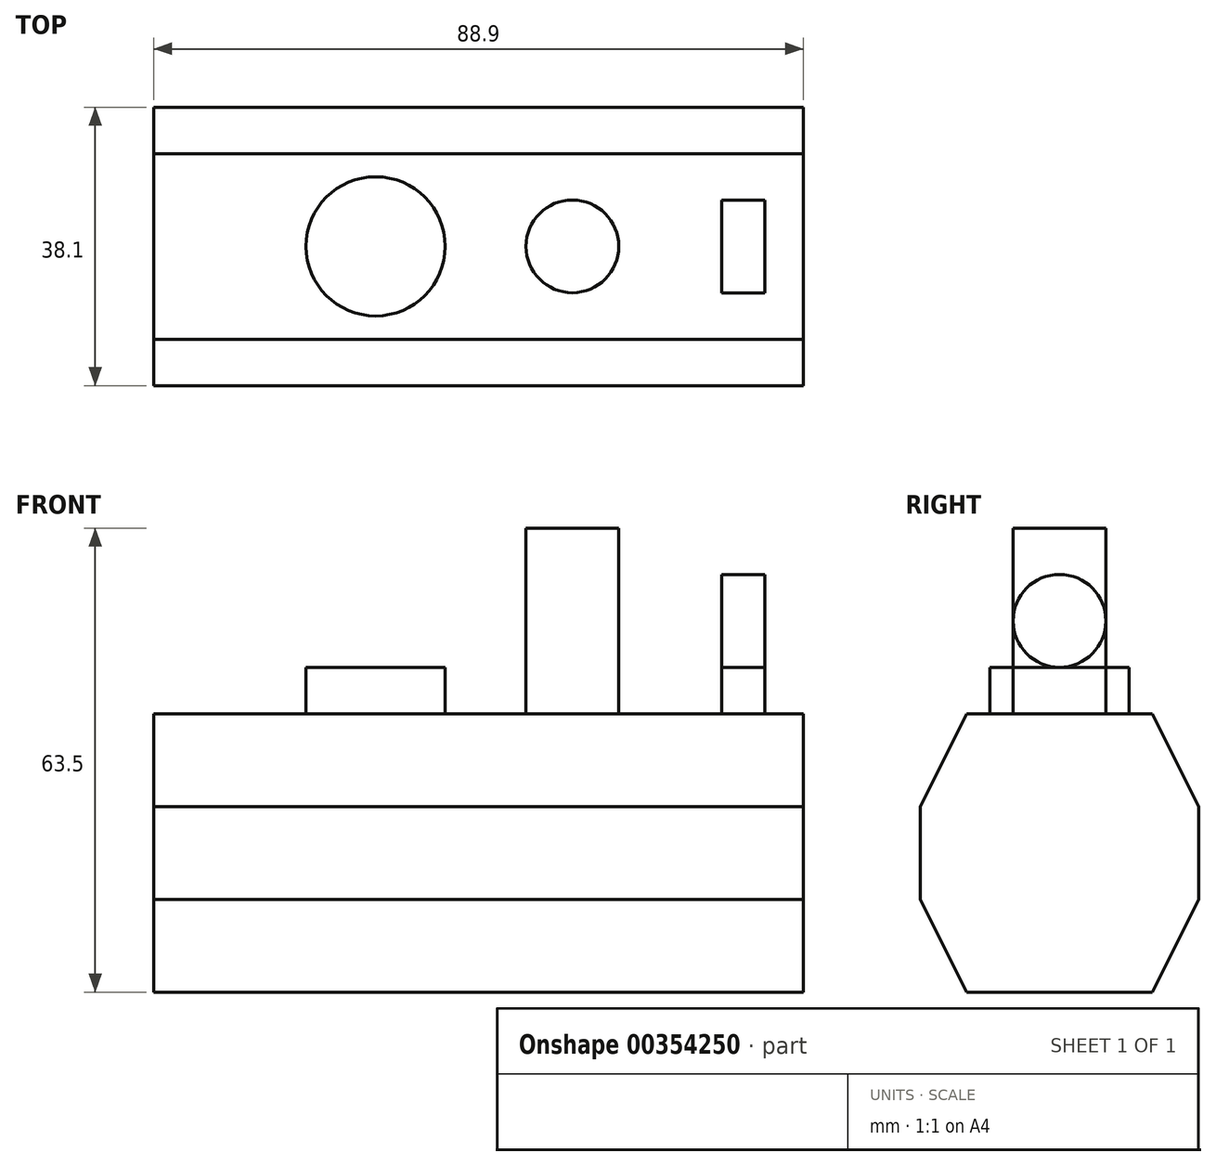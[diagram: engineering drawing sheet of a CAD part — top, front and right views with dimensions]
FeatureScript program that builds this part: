
annotation { "Feature Type Name" : "Feature", "Feature Type Description" : "" }
export const myFeature = defineFeature(function(context is Context, id is Id, definition is map)
    precondition{}
    {
        {
            var Q0;
            Q0=qCreatedBy(makeId("Front.planeOp"),FACE);
            var sketch = newSketch(context, id + "F0", { "sketchPlane" : qUnion([Q0])});
            skLineSegment(sketch, "E0.bottom", {"start": v(-41.2, 31.8) * mm, "end": v(47.7, 31.8) * mm});
            skLineSegment(sketch, "E0.top", {"start": v(-41.2, -6.3) * mm, "end": v(47.7, -6.3) * mm});
            skLineSegment(sketch, "E0.left", {"start": v(-41.2, 31.8) * mm, "end": v(-41.2, -6.3) * mm});
            skLineSegment(sketch, "E0.right", {"start": v(47.7, 31.8) * mm, "end": v(47.7, -6.3) * mm});
            skSolve(sketch);
        }
        {
            var Q0;
            Q0 = qSketchRegion(id + "F0", true);
            extrude(context, id + "F1", {"entities" : qUnion([Q0]), "depth" : 38.1 * mm});
        }
        {
            var Q0;
            Q0=makeQuery(id+"F1.opExtrude","SWEPT_FACE",FACE,{"disambiguationData":[OSD([sQuery(id+"F0.wireOp",EDGE,"E0.left")])]});
            var sketch = newSketch(context, id + "F2", { "sketchPlane" : qUnion([Q0])});
            skLineSegment(sketch, "E1", {"start": v(0, 19.1) * mm, "end": v(6.35, 31.8) * mm});
            skLineSegment(sketch, "E2", {"start": v(31.75, 31.8) * mm, "end": v(38.1, 19.1) * mm});
            skLineSegment(sketch, "E3", {"start": v(0, 6.4) * mm, "end": v(6.35, -6.3) * mm});
            skLineSegment(sketch, "E4", {"start": v(38.1, 6.4) * mm, "end": v(31.75, -6.3) * mm});
            skSolve(sketch);
        }
        {
            var Q0;
            {var subQ0=sQuery(id+"F2.wireOp",EDGE,"E1");Q0=makeQuery(id+"F2.imprint","IMPRINT",FACE,{"disambiguationData":[TD([[makeQuery(id+"F2.imprint","IMPRINT",EDGE,{"derivedFrom":subQ0}),1.0]])]});}
            var Q1;
            {var subQ0=sQuery(id+"F2.wireOp",EDGE,"E3");Q1=makeQuery(id+"F2.imprint","IMPRINT",FACE,{"disambiguationData":[TD([[makeQuery(id+"F2.imprint","IMPRINT",EDGE,{"derivedFrom":subQ0}),-1.0]])]});}
            var Q2;
            {var subQ0=sQuery(id+"F2.wireOp",EDGE,"E4");Q2=makeQuery(id+"F2.imprint","IMPRINT",FACE,{"disambiguationData":[TD([[makeQuery(id+"F2.imprint","IMPRINT",EDGE,{"derivedFrom":subQ0}),1.0]])]});}
            var Q3;
            {var subQ0=sQuery(id+"F2.wireOp",EDGE,"E2");Q3=makeQuery(id+"F2.imprint","IMPRINT",FACE,{"disambiguationData":[TD([[makeQuery(id+"F2.imprint","IMPRINT",EDGE,{"derivedFrom":subQ0}),1.0]])]});}
            extrude(context, id + "F3", {"entities" : qUnion([Q0, Q1, Q2, Q3]), "operationType" : NewBodyOperationType.REMOVE, "endBound" : BoundingType.THROUGH_ALL, "oppositeDirection" : true, "depth" : 25.4 * mm});
        }
        {
            var Q0;
            Q0=makeQuery(id+"F1.opExtrude","SWEPT_FACE",FACE,{"disambiguationData":[OSD([sQuery(id+"F0.wireOp",EDGE,"E0.bottom")])]});
            var sketch = newSketch(context, id + "F4", { "sketchPlane" : qUnion([Q0])});
            skCircle(sketch, "E5", {"center": v(16.1, -19.05) * mm, "radius": 6.35 * mm});
            skCircle(sketch, "E6", {"center": v(-10.83, -19.05) * mm, "radius": 9.53 * mm});
            skLineSegment(sketch, "E7.bottom", {"start": v(36.52, -12.7) * mm, "end": v(42.4, -12.7) * mm});
            skLineSegment(sketch, "E7.top", {"start": v(36.52, -25.4) * mm, "end": v(42.4, -25.4) * mm});
            skLineSegment(sketch, "E7.left", {"start": v(36.52, -12.7) * mm, "end": v(36.52, -25.4) * mm});
            skLineSegment(sketch, "E7.right", {"start": v(42.4, -12.7) * mm, "end": v(42.4, -25.4) * mm});
            skSolve(sketch);
        }
        {
            var Q0;
            Q0=makeQuery(id+"F4.imprint","IMPRINT",FACE,{"disambiguationData":[TD([[makeQuery(id+"F4.imprint","IMPRINT",EDGE,{"derivedFrom":sQuery(id+"F4.wireOp",EDGE,"E5")}),1.0]])]});
            extrude(context, id + "F5", {"entities" : qUnion([Q0]), "operationType" : NewBodyOperationType.ADD, "depth" : 25.4 * mm});
        }
        {
            var Q0;
            Q0=makeQuery(id+"F4.imprint","IMPRINT",FACE,{"disambiguationData":[TD([[makeQuery(id+"F4.imprint","IMPRINT",EDGE,{"derivedFrom":sQuery(id+"F4.wireOp",EDGE,"E6")}),1.0]])]});
            extrude(context, id + "F6", {"entities" : qUnion([Q0]), "operationType" : NewBodyOperationType.ADD, "depth" : 6.35 * mm});
        }
        {
            var Q0;
            Q0=makeQuery(id+"F4.imprint","IMPRINT",FACE,{"disambiguationData":[TD([[makeQuery(id+"F4.imprint","IMPRINT",EDGE,{"derivedFrom":sQuery(id+"F4.wireOp",EDGE,"E7.bottom")}),-1.0]])]});
            extrude(context, id + "F7", {"entities" : qUnion([Q0]), "operationType" : NewBodyOperationType.ADD, "depth" : 19.05 * mm});
        }
        {
            var Q0;
            Q0=makeQuery(id+"F7.opExtrude","SWEPT_FACE",FACE,{"disambiguationData":[OSD([sQuery(id+"F4.wireOp",EDGE,"E7.right")])]});
            var sketch = newSketch(context, id + "F8", { "sketchPlane" : qUnion([Q0])});
            skLineSegment(sketch, "E8", {"start": v(-25.4, 38.15) * mm, "end": v(-12.7, 38.15) * mm});
            skCircle(sketch, "E9", {"center": v(-19.05, 44.5) * mm, "radius": 6.35 * mm});
            skPoint(sketch, "E9.centerSnap0", {"position": v(-19.05, 50.85) * mm});
            skSolve(sketch);
        }
        {
            var Q0;
            {var subQ0=sQuery(id+"F8.wireOp",EDGE,"E9");var subQ1=sQuery(id+"F4.wireOp",EDGE,"E7.right");var subQ2=makeQuery(id+"F7.opExtrude","CAP_EDGE",EDGE,{"disambiguationData":[OSD([subQ1])],"isStart":false});var subQ3=makeQuery(id+"F8.imprint","INTERSECT",VERTEX,{"derivedFrom":[subQ2,subQ0]});Q0=makeQuery(id+"F8.imprint","IMPRINT",FACE,{"disambiguationData":[TD([[makeQuery(id+"F8.imprint","IMPRINT",EDGE,{"disambiguationData":[TD([[subQ3,1.0]])],"derivedFrom":subQ0}),-1.0]])]});}
            var Q1;
            {var subQ0=sQuery(id+"F8.wireOp",EDGE,"E8");var subQ3=sQuery(id+"F8.wireOp",EDGE,"E9");var subQ4=makeQuery(id+"F8.imprint","INTERSECT",VERTEX,{"derivedFrom":[subQ0,subQ3]});Q1=makeQuery(id+"F8.imprint","IMPRINT",FACE,{"disambiguationData":[TD([[makeQuery(id+"F8.imprint","IMPRINT",EDGE,{"disambiguationData":[TD([[subQ4,-1.0]])],"derivedFrom":subQ0}),1.0]])]});}
            var Q2;
            {var subQ0=sQuery(id+"F8.wireOp",EDGE,"E8");var subQ3=sQuery(id+"F8.wireOp",EDGE,"E9");var subQ4=makeQuery(id+"F8.imprint","INTERSECT",VERTEX,{"derivedFrom":[subQ0,subQ3]});Q2=makeQuery(id+"F8.imprint","IMPRINT",FACE,{"disambiguationData":[TD([[makeQuery(id+"F8.imprint","IMPRINT",EDGE,{"disambiguationData":[TD([[subQ4,1.0]])],"derivedFrom":subQ0}),1.0]])]});}
            var Q3;
            {var subQ0=sQuery(id+"F8.wireOp",EDGE,"E9");var subQ1=sQuery(id+"F4.wireOp",EDGE,"E7.right");var subQ2=makeQuery(id+"F7.opExtrude","CAP_EDGE",EDGE,{"disambiguationData":[OSD([subQ1])],"isStart":false});var subQ3=makeQuery(id+"F8.imprint","INTERSECT",VERTEX,{"derivedFrom":[subQ2,subQ0]});Q3=makeQuery(id+"F8.imprint","IMPRINT",FACE,{"disambiguationData":[TD([[makeQuery(id+"F8.imprint","IMPRINT",EDGE,{"disambiguationData":[TD([[subQ3,-1.0]])],"derivedFrom":subQ0}),-1.0]])]});}
            extrude(context, id + "F9", {"entities" : qUnion([Q0, Q1, Q2, Q3]), "operationType" : NewBodyOperationType.REMOVE, "endBound" : BoundingType.UP_TO_NEXT, "oppositeDirection" : true, "depth" : 25.4 * mm});
        }
    });
